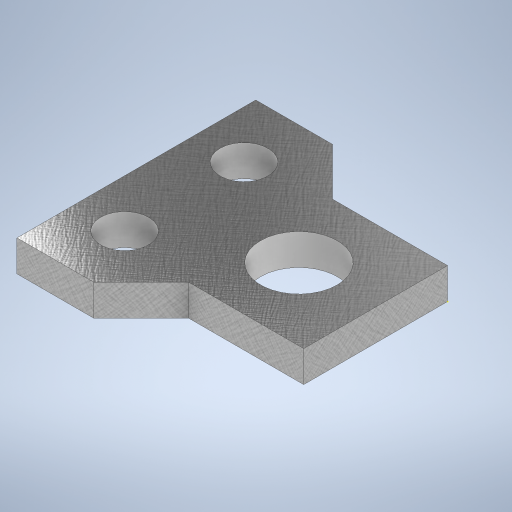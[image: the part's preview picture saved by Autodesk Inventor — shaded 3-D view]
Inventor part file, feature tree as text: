
AUTODESK INVENTOR PART (.ipt)
format: ipt  version: 2024 (Build 280153000, 153)  size: 324,608 bytes
history: native  units: mm
features: sketch x2, extrude x2
ambient origin geometry x8: Origin, YZ Plane, XZ Plane, XY Plane, X Axis, Y Axis, Z Axis, Center Point
bodies: Solid1 (feature_tree)
feature tree (4):
  sketch  "Sketch1"  dims[d2=15.0mm d3=12.0mm]
  sketch  "Sketch2"  dims[d4=7.0mm d5=45.0deg d6=8.0mm d7=3.25mm d8=0.0mm d9=8.0mm d10=8.0mm d11=5.0mm d12=5.0mm d13=3.25mm d14=0.0mm]
  extrude  "Extrusion1"  Depth=12.0mm
  extrude  "Extrusion2"  TaperAngle=45.0deg  [1 undecoded]
note: 1 required parameter value undecoded (feature->parameter linkage not recoverable at this tier; creation-order binding heuristic only, values carry confidence <= 0.55)
